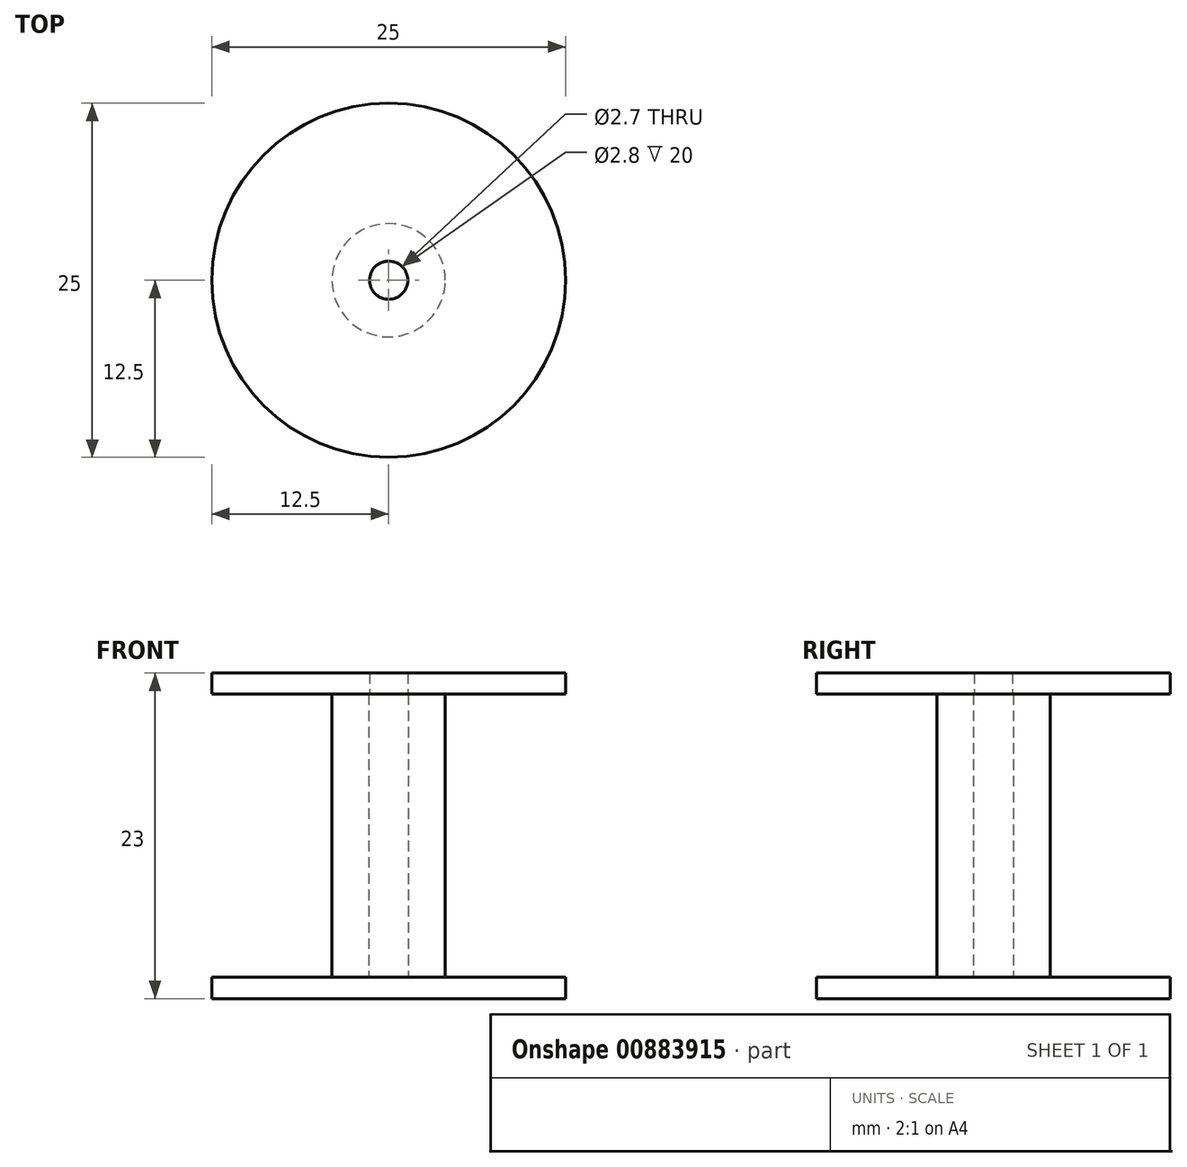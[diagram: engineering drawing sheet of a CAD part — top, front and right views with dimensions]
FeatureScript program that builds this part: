
annotation { "Feature Type Name" : "Feature", "Feature Type Description" : "" }
export const myFeature = defineFeature(function(context is Context, id is Id, definition is map)
    precondition{}
    {
        {
            var Q0;
            Q0=qCreatedBy(makeId("Top.planeOp"),FACE);
            var sketch = newSketch(context, id + "F0", { "sketchPlane" : qUnion([Q0])});
            skCircle(sketch, "E0", {"center": v(0, 0) * mm, "radius": 12.5 * mm});
            skSolve(sketch);
        }
        {
            var Q0;
            Q0 = qSketchRegion(id + "F0", true);
            extrude(context, id + "F1", {"entities" : qUnion([Q0]), "depth" : 1.5 * mm, "offsetDistance" : 25 * mm});
        }
        {
            var Q0;
            Q0=makeQuery(id+"F1.opExtrude","CAP_FACE",FACE,{"disambiguationData":[OSD([sQuery(id+"F0.wireOp",EDGE,"E0")])],"isStart":false});
            var sketch = newSketch(context, id + "F2", { "sketchPlane" : qUnion([Q0])});
            skCircle(sketch, "E1", {"center": v(0, 0) * mm, "radius": 1.4 * mm});
            skCircle(sketch, "E2", {"center": v(0, 0) * mm, "radius": 4 * mm});
            skSolve(sketch);
        }
        {
            var Q0;
            Q0 = qSketchRegion(id + "F2", true);
            extrude(context, id + "F3", {"entities" : qUnion([Q0]), "operationType" : NewBodyOperationType.ADD, "depth" : 20 * mm, "offsetDistance" : 25 * mm});
        }
        {
            var Q0;
            Q0=makeQuery(id+"F3.opExtrude","CAP_FACE",FACE,{"disambiguationData":[OSD([sQuery(id+"F2.wireOp",EDGE,"E1"),sQuery(id+"F2.wireOp",EDGE,"E2")])],"isStart":false});
            var sketch = newSketch(context, id + "F4", { "sketchPlane" : qUnion([Q0])});
            skCircle(sketch, "E3", {"center": v(0, 0) * mm, "radius": 12.5 * mm});
            skCircle(sketch, "E4", {"center": v(0, 0) * mm, "radius": 1.35 * mm});
            skSolve(sketch);
        }
        {
            var Q0;
            Q0 = qSketchRegion(id + "F4", true);
            extrude(context, id + "F5", {"entities" : qUnion([Q0]), "depth" : 1.5 * mm, "offsetDistance" : 25 * mm});
        }
    });
